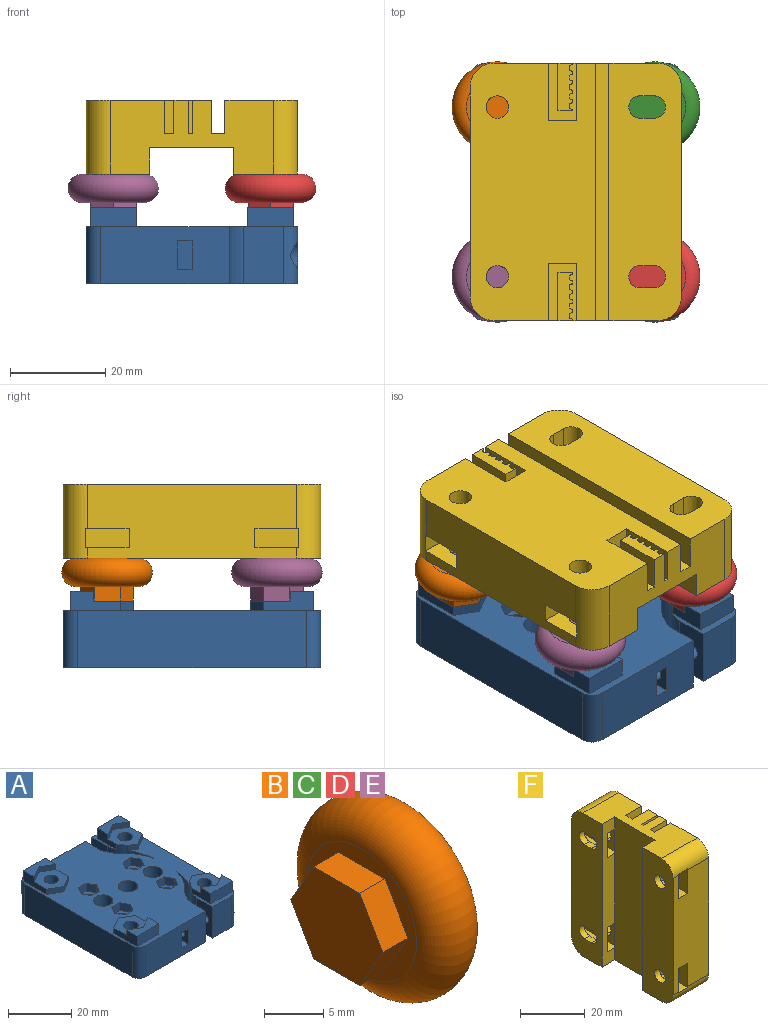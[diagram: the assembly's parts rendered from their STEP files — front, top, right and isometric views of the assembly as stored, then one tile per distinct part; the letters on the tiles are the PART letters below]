
ASSEMBLY  parts=6 mates=5
PART A: 125 faces, bbox 44.4x54x16 mm
  f0: plane 54x44.4mm, normal (0,0,1), area 1629.7mm2, adj f1,f3,f4,f5,f6,f7,f8,f9
  f1: plane 48x12mm, normal (1,0,0), area 542.9mm2, adj f0,f14,f41,f43,f82,f84
  f2: cylinder r=1.6mm len=6.4mm, axis (-1,0,0), area 64.3mm2, adj f6,f42
  f3: plane 27x12mm, normal (0,-1,0), area 306mm2, adj f0,f9,f14,f33,f34,f35,f36,f44
  f4: cylinder r=18.76mm len=14mm, axis (0,0,1), area 125.4mm2, adj f0,f5,f12,f14,f18,f19
  f5: cylinder r=8.26mm len=14mm, axis (0,0,1), area 78.6mm2, adj f0,f4,f6,f14,f15,f19
  f6: plane 12x7mm, normal (-1,0,0), area 76mm2, adj f0,f2,f5,f7,f14
  f7: plane 12x8.4mm, normal (0,-1,0), area 100.8mm2, adj f0,f6,f14,f43
  f8: plane 48x12mm, normal (-1,0,0), area 576mm2, adj f0,f14,f44,f85
  f9: plane 12x7mm, normal (1,0,0), area 76mm2, adj f0,f3,f10,f14,f40
  f10: cylinder r=14.58mm len=12mm, axis (0,0,1), area 107.2mm2, adj f0,f9,f12,f14
  f11: cylinder r=2.3mm len=12mm, axis (0,0,1), area 173.4mm2, adj f19,f86
  f12: cylinder r=16.31mm len=12mm, axis (0,0,1), area 104.2mm2, adj f0,f4,f10,f14
  f13: cylinder r=2.3mm len=12mm, axis (0,0,1), area 173.4mm2, adj f24,f89
  f14: plane 54x44.4mm, normal (0,0,-1), area 1937.3mm2, adj f1,f3,f4,f5,f6,f7,f8,f9
  f15: plane 8.5x4mm, normal (-1,0,0), area 26.6mm2, adj f0,f5,f19,f29,f31,f32
  f16: plane 10.4x4mm, normal (1,0,0), area 30.4mm2, adj f0,f17,f19,f30,f31,f32
  f17: plane 4.85x2.8mm, normal (0.5,0.87,0), area 11.2mm2, adj f0,f16,f18,f19
  f18: plane 2.58x2mm, normal (-0.5,0.87,0), area 6mm2, adj f0,f4,f17,f19
  f19: plane 11.2x9.7mm, normal (0,0,1), area 62.8mm2, adj f4,f5,f11,f15,f16,f17,f18,f29
  f20: plane 4.85x2.8mm, normal (0.5,0.87,0), area 11.2mm2, adj f0,f21,f23,f24
  f21: plane 4.85x2.8mm, normal (-0.5,0.87,0), area 11.2mm2, adj f0,f20,f22,f24
  f22: plane 10.4x4mm, normal (-1,0,0), area 30.4mm2, adj f0,f21,f24,f25,f27,f28
  f23: plane 10.4x4mm, normal (1,0,0), area 30.4mm2, adj f0,f20,f24,f26,f27,f28
  f24: plane 11.2x9.7mm, normal (0,0,1), area 64.9mm2, adj f13,f20,f21,f22,f23,f25,f26
  f25: plane 4.85x2.8mm, normal (0.5,0.87,0), area 11.2mm2, adj f22,f24,f26,f28
  f26: plane 4.85x2.8mm, normal (-0.5,0.87,0), area 11.2mm2, adj f23,f24,f25,f28
  f27: plane 9.7x4mm, normal (0,-1,0), area 38.8mm2, adj f0,f22,f23,f28
  f28: plane 9.7x4.8mm, normal (0,0,1), area 33mm2, adj f22,f23,f25,f26,f27
  f29: plane 4.85x2.8mm, normal (0.5,0.87,0), area 11.2mm2, adj f15,f19,f30,f32
  f30: plane 4.85x2.8mm, normal (-0.5,0.87,0), area 11.2mm2, adj f16,f19,f29,f32
  f31: plane 9.7x4mm, normal (0,-1,0), area 38.8mm2, adj f0,f15,f16,f32
  f32: plane 9.7x4.8mm, normal (0,0,1), area 33mm2, adj f15,f16,f29,f30,f31
  f33: plane 6.8x3mm, normal (0,0,1), area 20.4mm2, adj f3,f34,f36,f37
  f34: plane 6.8x6mm, normal (-1,0,0), area 32.8mm2, adj f3,f33,f35,f37,f40
  f35: plane 6.8x3mm, normal (0,0,-1), area 20.4mm2, adj f3,f34,f36,f37
  f36: plane 6.8x6mm, normal (1,0,0), area 32.8mm2, adj f3,f33,f35,f37,f39
  f37: plane 6x3mm, normal (0,-1,0), area 18mm2, adj f33,f34,f35,f36
  f38: plane 3.2x3.2mm, normal (1,0,0), area 8mm2, adj f39
  f39: cylinder r=1.6mm len=6mm, axis (-1,0,0), area 60.3mm2, adj f36,f38
  f40: cylinder r=1.6mm len=7.8mm, axis (-1,0,0), area 78.4mm2, adj f9,f34
  f41: cylinder r=3mm len=6mm, axis (1,0,0), area 88.2mm2, adj f1,f42,f43
  f42: plane 6x6mm, normal (1,0,0), area 20.2mm2, adj f2,f41
  f43: cylinder r=3mm len=12mm, axis (0,0,-1), area 43.2mm2, adj f0,f1,f7,f14,f41
  f44: cylinder r=3mm len=12mm, axis (0,0,1), area 56.5mm2, adj f0,f3,f8,f14
  f45: cylinder r=1.6mm len=6.4mm, axis (-1,0,0), area 64.3mm2, adj f49,f83
  f46: plane 27x12mm, normal (0,1,0), area 306mm2, adj f0,f14,f51,f74,f75,f76,f77,f85
  f47: cylinder r=18.76mm len=14mm, axis (0,0,1), area 125.4mm2, adj f0,f14,f48,f54,f59,f60
  f48: cylinder r=8.26mm len=14mm, axis (0,0,1), area 78.6mm2, adj f0,f14,f47,f49,f56,f60
  f49: plane 12x7mm, normal (-1,0,0), area 76mm2, adj f0,f14,f45,f48,f50
  f50: plane 12x8.4mm, normal (0,1,0), area 100.8mm2, adj f0,f14,f49,f84
  f51: plane 12x7mm, normal (1,0,0), area 76mm2, adj f0,f14,f46,f52,f81
  f52: cylinder r=14.58mm len=12mm, axis (0,0,1), area 107.2mm2, adj f0,f14,f51,f54
  f53: cylinder r=2.3mm len=12mm, axis (0,0,1), area 173.4mm2, adj f60,f87
  f54: cylinder r=16.31mm len=12mm, axis (0,0,1), area 104.2mm2, adj f0,f14,f47,f52
  f55: cylinder r=2.3mm len=12mm, axis (0,0,1), area 173.4mm2, adj f65,f88
  f56: plane 8.5x4mm, normal (-1,0,0), area 26.6mm2, adj f0,f48,f60,f70,f72,f73
  f57: plane 10.4x4mm, normal (1,0,0), area 30.4mm2, adj f0,f58,f60,f71,f72,f73
  f58: plane 4.85x2.8mm, normal (0.5,-0.87,0), area 11.2mm2, adj f0,f57,f59,f60
  f59: plane 2.58x2mm, normal (-0.5,-0.87,0), area 6mm2, adj f0,f47,f58,f60
  f60: plane 11.2x9.7mm, normal (0,0,1), area 62.8mm2, adj f47,f48,f53,f56,f57,f58,f59,f70
  f61: plane 4.85x2.8mm, normal (0.5,-0.87,0), area 11.2mm2, adj f0,f62,f64,f65
  f62: plane 4.85x2.8mm, normal (-0.5,-0.87,0), area 11.2mm2, adj f0,f61,f63,f65
  f63: plane 10.4x4mm, normal (-1,0,0), area 30.4mm2, adj f0,f62,f65,f66,f68,f69
  f64: plane 10.4x4mm, normal (1,0,0), area 30.4mm2, adj f0,f61,f65,f67,f68,f69
  f65: plane 11.2x9.7mm, normal (0,0,1), area 64.9mm2, adj f55,f61,f62,f63,f64,f66,f67
  f66: plane 4.85x2.8mm, normal (0.5,-0.87,0), area 11.2mm2, adj f63,f65,f67,f69
  f67: plane 4.85x2.8mm, normal (-0.5,-0.87,0), area 11.2mm2, adj f64,f65,f66,f69
  f68: plane 9.7x4mm, normal (0,1,0), area 38.8mm2, adj f0,f63,f64,f69
  f69: plane 9.7x4.8mm, normal (0,0,1), area 33mm2, adj f63,f64,f66,f67,f68
  f70: plane 4.85x2.8mm, normal (0.5,-0.87,0), area 11.2mm2, adj f56,f60,f71,f73
  f71: plane 4.85x2.8mm, normal (-0.5,-0.87,0), area 11.2mm2, adj f57,f60,f70,f73
  f72: plane 9.7x4mm, normal (0,1,0), area 38.8mm2, adj f0,f56,f57,f73
  f73: plane 9.7x4.8mm, normal (0,0,1), area 33mm2, adj f56,f57,f70,f71,f72
  f74: plane 6.8x3mm, normal (0,0,1), area 20.4mm2, adj f46,f75,f77,f78
  f75: plane 6.8x6mm, normal (-1,0,0), area 32.8mm2, adj f46,f74,f76,f78,f81
  f76: plane 6.8x3mm, normal (0,0,-1), area 20.4mm2, adj f46,f75,f77,f78
  f77: plane 6.8x6mm, normal (1,0,0), area 32.8mm2, adj f46,f74,f76,f78,f80
  f78: plane 6x3mm, normal (0,1,0), area 18mm2, adj f74,f75,f76,f77
  f79: plane 3.2x3.2mm, normal (1,0,0), area 8mm2, adj f80
  f80: cylinder r=1.6mm len=6mm, axis (-1,0,0), area 60.3mm2, adj f77,f79
  f81: cylinder r=1.6mm len=7.8mm, axis (-1,0,0), area 78.4mm2, adj f51,f75
  f82: cylinder r=3mm len=6mm, axis (1,0,0), area 88.2mm2, adj f1,f83,f84
  f83: plane 6x6mm, normal (1,0,0), area 20.2mm2, adj f45,f82
  f84: cylinder r=3mm len=12mm, axis (0,0,-1), area 43.2mm2, adj f0,f1,f14,f50,f82
  f85: cylinder r=3mm len=12mm, axis (0,0,1), area 56.5mm2, adj f0,f8,f14,f46
  f86: cone r=4.3mm half-angle=45deg, axis (0,0,-1), area 58.6mm2, adj f11,f14
  f87: cone r=2.3mm half-angle=45deg, axis (0,0,-1), area 58.6mm2, adj f14,f53
  f88: cone r=2.3mm half-angle=45deg, axis (0,0,-1), area 58.6mm2, adj f14,f55
  f89: cone r=4.3mm half-angle=45deg, axis (0,0,-1), area 58.6mm2, adj f13,f14
  f90: plane 3x3mm, normal (-0.87,0.5,0), area 10.4mm2, adj f0,f91,f95,f96
  f91: plane 3x3mm, normal (-0.87,-0.5,0), area 10.4mm2, adj f0,f90,f92,f96
  f92: plane 3.46x3mm, normal (0,-1,0), area 10.4mm2, adj f0,f91,f93,f96
  f93: plane 3x3mm, normal (0.87,-0.5,0), area 10.4mm2, adj f0,f92,f94,f96
  f94: plane 3x3mm, normal (0.87,0.5,0), area 10.4mm2, adj f0,f93,f95,f96
  f95: plane 3.46x3mm, normal (0,1,0), area 10.4mm2, adj f0,f90,f94,f96
  f96: plane 6.93x6mm, normal (0,0,1), area 21.6mm2, adj f90,f91,f92,f93,f94,f95,f118
  f97: plane 3x3mm, normal (0.87,-0.5,0), area 10.4mm2, adj f0,f98,f102,f103
  f98: plane 3x3mm, normal (0.87,0.5,0), area 10.4mm2, adj f0,f97,f99,f103
  f99: plane 3.46x3mm, normal (0,1,0), area 10.4mm2, adj f0,f98,f100,f103
  f100: plane 3x3mm, normal (-0.87,0.5,0), area 10.4mm2, adj f0,f99,f101,f103
  f101: plane 3x3mm, normal (-0.87,-0.5,0), area 10.4mm2, adj f0,f100,f102,f103
  f102: plane 3.46x3mm, normal (0,-1,0), area 10.4mm2, adj f0,f97,f101,f103
  f103: plane 6.93x6mm, normal (0,0,1), area 21.6mm2, adj f97,f98,f99,f100,f101,f102,f121
  f104: plane 3x3mm, normal (0.87,-0.5,0), area 10.4mm2, adj f0,f105,f109,f110
  f105: plane 3x3mm, normal (0.87,0.5,0), area 10.4mm2, adj f0,f104,f106,f110
  f106: plane 3.46x3mm, normal (0,1,0), area 10.4mm2, adj f0,f105,f107,f110
  f107: plane 3x3mm, normal (-0.87,0.5,0), area 10.4mm2, adj f0,f106,f108,f110
  f108: plane 3x3mm, normal (-0.87,-0.5,0), area 10.4mm2, adj f0,f107,f109,f110
  f109: plane 3.46x3mm, normal (0,-1,0), area 10.4mm2, adj f0,f104,f108,f110
  f110: plane 6.93x6mm, normal (0,0,1), area 21.6mm2, adj f104,f105,f106,f107,f108,f109,f120
  f111: plane 3x3mm, normal (-0.87,0.5,0), area 10.4mm2, adj f0,f112,f116,f117
  f112: plane 3x3mm, normal (-0.87,-0.5,0), area 10.4mm2, adj f0,f111,f113,f117
  f113: plane 3.46x3mm, normal (0,-1,0), area 10.4mm2, adj f0,f112,f114,f117
  f114: plane 3x3mm, normal (0.87,-0.5,0), area 10.4mm2, adj f0,f113,f115,f117
  f115: plane 3x3mm, normal (0.87,0.5,0), area 10.4mm2, adj f0,f114,f116,f117
  f116: plane 3.46x3mm, normal (0,1,0), area 10.4mm2, adj f0,f111,f115,f117
  f117: plane 6.93x6mm, normal (0,0,1), area 21.6mm2, adj f111,f112,f113,f114,f115,f116,f119
  f118: cylinder r=1.75mm len=9mm, axis (0,0,1), area 99mm2, adj f14,f96
  f119: cylinder r=1.75mm len=9mm, axis (0,0,1), area 99mm2, adj f14,f117
  f120: cylinder r=1.75mm len=9mm, axis (0,0,1), area 99mm2, adj f14,f110
  f121: cylinder r=1.75mm len=9mm, axis (0,0,1), area 99mm2, adj f14,f103
  f122: cylinder r=3.1mm len=12mm, axis (0,0,-1), area 233.7mm2, adj f0,f14
  f123: cylinder r=3.1mm len=12mm, axis (0,0,-1), area 233.7mm2, adj f0,f14
  f124: cylinder r=3.1mm len=12mm, axis (0,0,-1), area 233.7mm2, adj f0,f14
PART B: 10 faces, bbox 9x20.6x20.6 mm
  f0: plane 13x13mm, normal (-1,0,0), area 54.6mm2, adj f1,f3,f4,f5,f6,f7,f8
  f1: torus R=6.5mm, axis (1,0,0), area 498mm2, adj f0,f2
  f2: plane 13x13mm, normal (1,0,0), area 132.7mm2, adj f1
  f3: plane 4.75x3mm, normal (0,0.87,0.5), area 16.5mm2, adj f0,f4,f8,f9
  f4: plane 4.75x3mm, normal (0,0.87,-0.5), area 16.5mm2, adj f0,f3,f5,f9
  f5: plane 5.49x3mm, normal (0,0,-1), area 16.5mm2, adj f0,f4,f6,f9
  f6: plane 4.75x3mm, normal (0,-0.87,-0.5), area 16.5mm2, adj f0,f5,f7,f9
  f7: plane 4.75x3mm, normal (0,-0.87,0.5), area 16.5mm2, adj f0,f6,f8,f9
  f8: plane 5.49x3mm, normal (0,0,1), area 16.5mm2, adj f0,f3,f7,f9
  f9: plane 10.97x9.5mm, normal (-1,0,0), area 78.2mm2, adj f3,f4,f5,f6,f7,f8
PART C: same geometry as B
PART D: same geometry as B
PART E: same geometry as B
PART F: 134 faces, bbox 15.5x44.3x54 mm
  f0: plane 54x13.33mm, normal (-1,0,0), area 646.2mm2, adj f7,f12,f13,f56,f67,f72,f110,f119
  f1: plane 13.33x9.2mm, normal (1,0,0), area 91.2mm2, adj f7,f13,f110,f111,f112,f119,f125,f126
  f2: plane 13.33x9.2mm, normal (-1,0,0), area 91.2mm2, adj f7,f69,f111,f112,f119,f120,f122,f123
  f3: plane 44x15.5mm, normal (0,-1,0), area 611.6mm2, adj f10,f15,f61,f62,f64,f66,f113,f114
  f4: cylinder r=2.35mm len=4.7mm, axis (-1,0,0), area 33.2mm2, adj f15,f61
  f5: cylinder r=2.35mm len=9.25mm, axis (-1,0,0), area 68.3mm2, adj f6,f58,f128,f130
  f6: plane 54x15.2mm, normal (1,0,0), area 747.2mm2, adj f5,f7,f12,f19,f67,f69,f72,f119
  f7: plane 44x15.5mm, normal (0,1,0), area 611.6mm2, adj f0,f1,f2,f6,f57,f58,f59,f67
  f8: plane 12.02x5.91mm, normal (1,0,0), area 44.5mm2, adj f12,f16,f17,f18,f22,f23,f24,f25
  f9: plane 10.02x3.1mm, normal (1,0,0), area 26.6mm2, adj f12,f18,f22,f23,f24,f25,f26,f27
  f10: plane 54x26.3mm, normal (1,0,0), area 1232.7mm2, adj f3,f12,f16,f17,f20,f54,f55,f66
  f11: plane 54x17.64mm, normal (-1,0,0), area 952.5mm2, adj f12,f13,f14,f72,f120,f121
  f12: plane 34.3x15.5mm, normal (0,0,-1), area 395.4mm2, adj f0,f6,f8,f9,f10,f11,f13,f14
  f13: plane 54x5.5mm, normal (0,-1,0), area 237.2mm2, adj f0,f1,f11,f12,f57,f59,f60,f72
  f14: plane 54x5.5mm, normal (0,1,0), area 297mm2, adj f11,f12,f15,f72
  f15: plane 54x13.33mm, normal (-1,0,0), area 674.4mm2, adj f3,f4,f12,f14,f66,f68,f72,f118
  f16: plane 12.02x7mm, normal (0,-1,0), area 84.2mm2, adj f8,f10,f12,f17
  f17: plane 7x5.91mm, normal (0,0,-1), area 41.3mm2, adj f8,f10,f16,f54
  f18: plane 7x0.13mm, normal (0,1,0), area 0.9mm2, adj f8,f9,f12,f38
  f19: plane 54x7mm, normal (0,-1,0), area 378mm2, adj f6,f12,f21,f72
  f20: plane 54x7mm, normal (0,1,0), area 378mm2, adj f10,f12,f21,f72
  f21: plane 54x2.8mm, normal (1,0,0), area 151.2mm2, adj f12,f19,f20,f72
  f22: plane 7x0.75mm, normal (0,1,0), area 5.2mm2, adj f8,f9,f23,f51
  f23: cylinder r=1.41mm len=7mm, axis (-1,0,0), area 4.8mm2, adj f8,f9,f22,f24
  f24: cylinder r=0.2mm len=7mm, axis (-1,0,0), area 1.9mm2, adj f8,f9,f23,f25
  f25: plane 7x0.26mm, normal (0,1,0), area 1.8mm2, adj f8,f9,f24,f26
  f26: cylinder r=0.2mm len=7mm, axis (-1,0,0), area 1.9mm2, adj f8,f9,f25,f27
  f27: cylinder r=1.41mm len=7mm, axis (-1,0,0), area 4.8mm2, adj f8,f9,f26,f28
  f28: plane 7x0.75mm, normal (0,1,0), area 5.2mm2, adj f8,f9,f27,f29
  f29: cylinder r=1.41mm len=7mm, axis (-1,0,0), area 4.8mm2, adj f8,f9,f28,f30
  f30: cylinder r=0.2mm len=7mm, axis (-1,0,0), area 1.9mm2, adj f8,f9,f29,f31
  f31: plane 7x0.26mm, normal (0,1,0), area 1.8mm2, adj f8,f9,f30,f32
  f32: cylinder r=0.2mm len=7mm, axis (-1,0,0), area 1.9mm2, adj f8,f9,f31,f33
  f33: cylinder r=1.41mm len=7mm, axis (-1,0,0), area 4.8mm2, adj f8,f9,f32,f34
  f34: plane 7x0.75mm, normal (0,1,0), area 5.2mm2, adj f8,f9,f33,f35
  f35: cylinder r=1.41mm len=7mm, axis (-1,0,0), area 4.8mm2, adj f8,f9,f34,f36
  f36: cylinder r=0.2mm len=7mm, axis (-1,0,0), area 1.9mm2, adj f8,f9,f35,f37
  f37: plane 7x0.15mm, normal (0,1,0), area 1.1mm2, adj f8,f9,f36,f52
  f38: cylinder r=0.2mm len=7mm, axis (-1,0,0), area 1.9mm2, adj f8,f9,f18,f39
  f39: cylinder r=1.41mm len=7mm, axis (-1,0,0), area 4.8mm2, adj f8,f9,f38,f40
  f40: plane 7x0.75mm, normal (0,1,0), area 5.2mm2, adj f8,f9,f39,f41
  f41: cylinder r=1.41mm len=7mm, axis (-1,0,0), area 4.8mm2, adj f8,f9,f40,f42
  f42: cylinder r=0.2mm len=7mm, axis (-1,0,0), area 1.9mm2, adj f8,f9,f41,f43
  f43: plane 7x0.26mm, normal (0,1,0), area 1.8mm2, adj f8,f9,f42,f44
  f44: cylinder r=0.2mm len=7mm, axis (-1,0,0), area 1.9mm2, adj f8,f9,f43,f45
  f45: cylinder r=1.41mm len=7mm, axis (-1,0,0), area 4.8mm2, adj f8,f9,f44,f46
  f46: plane 7x0.75mm, normal (0,1,0), area 5.2mm2, adj f8,f9,f45,f47
  f47: cylinder r=1.41mm len=7mm, axis (-1,0,0), area 4.8mm2, adj f8,f9,f46,f48
  f48: cylinder r=0.2mm len=7mm, axis (-1,0,0), area 1.9mm2, adj f8,f9,f47,f49
  f49: plane 7x0.26mm, normal (0,1,0), area 1.8mm2, adj f8,f9,f48,f50
  f50: cylinder r=0.2mm len=7mm, axis (-1,0,0), area 1.9mm2, adj f8,f9,f49,f51
  f51: cylinder r=1.41mm len=7mm, axis (-1,0,0), area 4.8mm2, adj f8,f9,f22,f50
  f52: plane 7x3.1mm, normal (0,0,1), area 21.7mm2, adj f8,f9,f37,f53
  f53: plane 10.02x7mm, normal (0,-1,0), area 70.1mm2, adj f8,f9,f12,f52
  f54: plane 12.02x7mm, normal (0,1,0), area 84.2mm2, adj f8,f10,f12,f17
  f55: cylinder r=2.35mm len=9.25mm, axis (-1,0,0), area 136.6mm2, adj f10,f62
  f56: cylinder r=2.35mm len=4.7mm, axis (-1,0,0), area 16.6mm2, adj f0,f57,f131,f133
  f57: plane 13.33x9.2mm, normal (1,0,0), area 91.2mm2, adj f7,f13,f56,f59,f60,f67,f131,f132
  f58: plane 13.33x9.2mm, normal (-1,0,0), area 91.2mm2, adj f5,f7,f59,f60,f67,f121,f128,f129
  f59: plane 13.33x4mm, normal (0,0,-1), area 53.3mm2, adj f7,f13,f57,f58,f121
  f60: plane 13.31x4mm, normal (0,0,1), area 53.3mm2, adj f13,f57,f58,f67,f121
  f61: plane 10.45x9.2mm, normal (1,0,0), area 78.8mm2, adj f3,f4,f63,f64,f65,f66
  f62: plane 10.45x9.2mm, normal (-1,0,0), area 78.8mm2, adj f3,f55,f63,f64,f65,f66
  f63: plane 10.43x4mm, normal (0,0,1), area 41.7mm2, adj f61,f62,f65,f66
  f64: plane 10.45x4mm, normal (0,0,-1), area 41.8mm2, adj f3,f61,f62,f65
  f65: plane 9.2x4mm, normal (0,-1,0), area 36.8mm2, adj f61,f62,f63,f64
  f66: cylinder r=5mm len=15.5mm, axis (-1,0,0), area 120.1mm2, adj f3,f10,f12,f15,f61,f62,f63
  f67: cylinder r=5mm len=15.5mm, axis (1,0,0), area 120.1mm2, adj f0,f6,f7,f12,f57,f58,f60
  f68: cylinder r=2.35mm len=4.7mm, axis (-1,0,0), area 33.2mm2, adj f15,f113
  f69: cylinder r=2.35mm len=9.25mm, axis (-1,0,0), area 68.3mm2, adj f2,f6,f122,f124
  f70: plane 12.02x5.91mm, normal (1,0,0), area 44.5mm2, adj f72,f73,f74,f75,f76,f77,f78,f79
  f71: plane 10.02x3.1mm, normal (1,0,0), area 26.6mm2, adj f72,f75,f76,f77,f78,f79,f80,f81
  f72: plane 34.3x15.5mm, normal (0,0,1), area 395.4mm2, adj f0,f6,f10,f11,f13,f14,f15,f19
  f73: plane 12.02x7mm, normal (0,-1,0), area 84.2mm2, adj f10,f70,f72,f74
  f74: plane 7x5.91mm, normal (0,0,1), area 41.3mm2, adj f10,f70,f73,f108
  f75: plane 7x0.13mm, normal (0,1,0), area 0.9mm2, adj f70,f71,f72,f92
  f76: plane 7x0.75mm, normal (0,1,0), area 5.2mm2, adj f70,f71,f77,f105
  f77: cylinder r=1.41mm len=7mm, axis (-1,0,0), area 4.8mm2, adj f70,f71,f76,f78
  f78: cylinder r=0.2mm len=7mm, axis (-1,0,0), area 1.9mm2, adj f70,f71,f77,f79
  f79: plane 7x0.26mm, normal (0,1,0), area 1.8mm2, adj f70,f71,f78,f80
  f80: cylinder r=0.2mm len=7mm, axis (-1,0,0), area 1.9mm2, adj f70,f71,f79,f81
  f81: cylinder r=1.41mm len=7mm, axis (-1,0,0), area 4.8mm2, adj f70,f71,f80,f82
  f82: plane 7x0.75mm, normal (0,1,0), area 5.2mm2, adj f70,f71,f81,f83
  f83: cylinder r=1.41mm len=7mm, axis (-1,0,0), area 4.8mm2, adj f70,f71,f82,f84
  f84: cylinder r=0.2mm len=7mm, axis (-1,0,0), area 1.9mm2, adj f70,f71,f83,f85
  f85: plane 7x0.26mm, normal (0,1,0), area 1.8mm2, adj f70,f71,f84,f86
  f86: cylinder r=0.2mm len=7mm, axis (-1,0,0), area 1.9mm2, adj f70,f71,f85,f87
  f87: cylinder r=1.41mm len=7mm, axis (-1,0,0), area 4.8mm2, adj f70,f71,f86,f88
  f88: plane 7x0.75mm, normal (0,1,0), area 5.2mm2, adj f70,f71,f87,f89
  f89: cylinder r=1.41mm len=7mm, axis (-1,0,0), area 4.8mm2, adj f70,f71,f88,f90
  f90: cylinder r=0.2mm len=7mm, axis (-1,0,0), area 1.9mm2, adj f70,f71,f89,f91
  f91: plane 7x0.15mm, normal (0,1,0), area 1.1mm2, adj f70,f71,f90,f106
  f92: cylinder r=0.2mm len=7mm, axis (-1,0,0), area 1.9mm2, adj f70,f71,f75,f93
  f93: cylinder r=1.41mm len=7mm, axis (-1,0,0), area 4.8mm2, adj f70,f71,f92,f94
  f94: plane 7x0.75mm, normal (0,1,0), area 5.2mm2, adj f70,f71,f93,f95
  f95: cylinder r=1.41mm len=7mm, axis (-1,0,0), area 4.8mm2, adj f70,f71,f94,f96
  f96: cylinder r=0.2mm len=7mm, axis (-1,0,0), area 1.9mm2, adj f70,f71,f95,f97
  f97: plane 7x0.26mm, normal (0,1,0), area 1.8mm2, adj f70,f71,f96,f98
  f98: cylinder r=0.2mm len=7mm, axis (-1,0,0), area 1.9mm2, adj f70,f71,f97,f99
  f99: cylinder r=1.41mm len=7mm, axis (-1,0,0), area 4.8mm2, adj f70,f71,f98,f100
  f100: plane 7x0.75mm, normal (0,1,0), area 5.2mm2, adj f70,f71,f99,f101
  f101: cylinder r=1.41mm len=7mm, axis (-1,0,0), area 4.8mm2, adj f70,f71,f100,f102
  f102: cylinder r=0.2mm len=7mm, axis (-1,0,0), area 1.9mm2, adj f70,f71,f101,f103
  f103: plane 7x0.26mm, normal (0,1,0), area 1.8mm2, adj f70,f71,f102,f104
  f104: cylinder r=0.2mm len=7mm, axis (-1,0,0), area 1.9mm2, adj f70,f71,f103,f105
  f105: cylinder r=1.41mm len=7mm, axis (-1,0,0), area 4.8mm2, adj f70,f71,f76,f104
  f106: plane 7x3.1mm, normal (0,0,-1), area 21.7mm2, adj f70,f71,f91,f107
  f107: plane 10.02x7mm, normal (0,-1,0), area 70.1mm2, adj f70,f71,f72,f106
  f108: plane 12.02x7mm, normal (0,1,0), area 84.2mm2, adj f10,f70,f72,f74
  f109: cylinder r=2.35mm len=9.25mm, axis (-1,0,0), area 136.6mm2, adj f10,f114
  f110: cylinder r=2.35mm len=4.7mm, axis (-1,0,0), area 16.6mm2, adj f0,f1,f125,f127
  f111: plane 13.33x4mm, normal (0,0,1), area 53.3mm2, adj f1,f2,f7,f13,f120
  f112: plane 13.31x4mm, normal (0,0,-1), area 53.3mm2, adj f1,f2,f13,f119,f120
  f113: plane 10.45x9.2mm, normal (1,0,0), area 78.8mm2, adj f3,f68,f115,f116,f117,f118
  f114: plane 10.45x9.2mm, normal (-1,0,0), area 78.8mm2, adj f3,f109,f115,f116,f117,f118
  f115: plane 10.43x4mm, normal (0,0,-1), area 41.7mm2, adj f113,f114,f117,f118
  f116: plane 10.45x4mm, normal (0,0,1), area 41.8mm2, adj f3,f113,f114,f117
  f117: plane 9.2x4mm, normal (0,-1,0), area 36.8mm2, adj f113,f114,f115,f116
  f118: cylinder r=5mm len=15.5mm, axis (-1,0,0), area 120.1mm2, adj f3,f10,f15,f72,f113,f114,f115
  f119: cylinder r=5mm len=15.5mm, axis (1,0,0), area 120.1mm2, adj f0,f1,f2,f6,f7,f72,f112
  f120: plane 9.2x0.75mm, normal (0,1,0), area 6.9mm2, adj f2,f11,f111,f112
  f121: plane 9.2x0.75mm, normal (0,1,0), area 6.9mm2, adj f11,f58,f59,f60
  f122: plane 9.25x3mm, normal (0,0,-1), area 27.7mm2, adj f2,f6,f69,f123
  f123: cylinder r=2.35mm len=9.25mm, axis (-1,0,0), area 68.3mm2, adj f2,f6,f122,f124
  f124: plane 9.25x3mm, normal (0,0,1), area 27.7mm2, adj f2,f6,f69,f123
  f125: plane 3x2.25mm, normal (0,0,1), area 6.8mm2, adj f0,f1,f110,f126
  f126: cylinder r=2.35mm len=4.7mm, axis (-1,0,0), area 16.6mm2, adj f0,f1,f125,f127
  f127: plane 3x2.25mm, normal (0,0,-1), area 6.8mm2, adj f0,f1,f110,f126
  f128: plane 9.25x3mm, normal (0,0,-1), area 27.7mm2, adj f5,f6,f58,f129
  f129: cylinder r=2.35mm len=9.25mm, axis (-1,0,0), area 68.3mm2, adj f6,f58,f128,f130
  f130: plane 9.25x3mm, normal (0,0,1), area 27.7mm2, adj f5,f6,f58,f129
  f131: plane 3x2.25mm, normal (0,0,1), area 6.8mm2, adj f0,f56,f57,f132
  f132: cylinder r=2.35mm len=4.7mm, axis (-1,0,0), area 16.6mm2, adj f0,f57,f131,f133
  f133: plane 3x2.25mm, normal (0,0,-1), area 6.8mm2, adj f0,f56,f57,f132
PLACE A t=(-21.7,12.45,-5.03)mm
PLACE B rot(axis=(0.71,0,0.71),180deg) t=(-75.7,-17.45,2.97)mm
PLACE C rot(axis=(0.71,0,0.71),180deg) t=(-42.7,-17.45,2.97)mm
PLACE D rot(axis=(0.71,0,0.71),180deg) t=(-42.7,-53.05,2.97)mm
PLACE E rot(axis=(0.71,0,0.71),180deg) t=(-75.7,-53.05,2.97)mm
PLACE F rot(axis=(-0.58,-0.58,-0.58),120deg) t=(-21.4,-55.2,1.77)mm
MATE fastened B.f1 <-> A.f55  axis (0,0,-1) through (-38.2,-0.75,-3.03)mm
MATE fastened B.f1 <-> F.f68  axis (0,0,1) through (-38.2,-0.75,5.97)mm
MATE fastened E.f1 <-> A.f13  axis (0,0,-1) through (-38.2,-36.35,-3.03)mm
MATE fastened C.f1 <-> A.f53  axis (0,0,-1) through (-5.2,-0.75,-3.03)mm
MATE fastened D.f1 <-> A.f11  axis (0,0,-1) through (-5.2,-36.35,-3.03)mm
